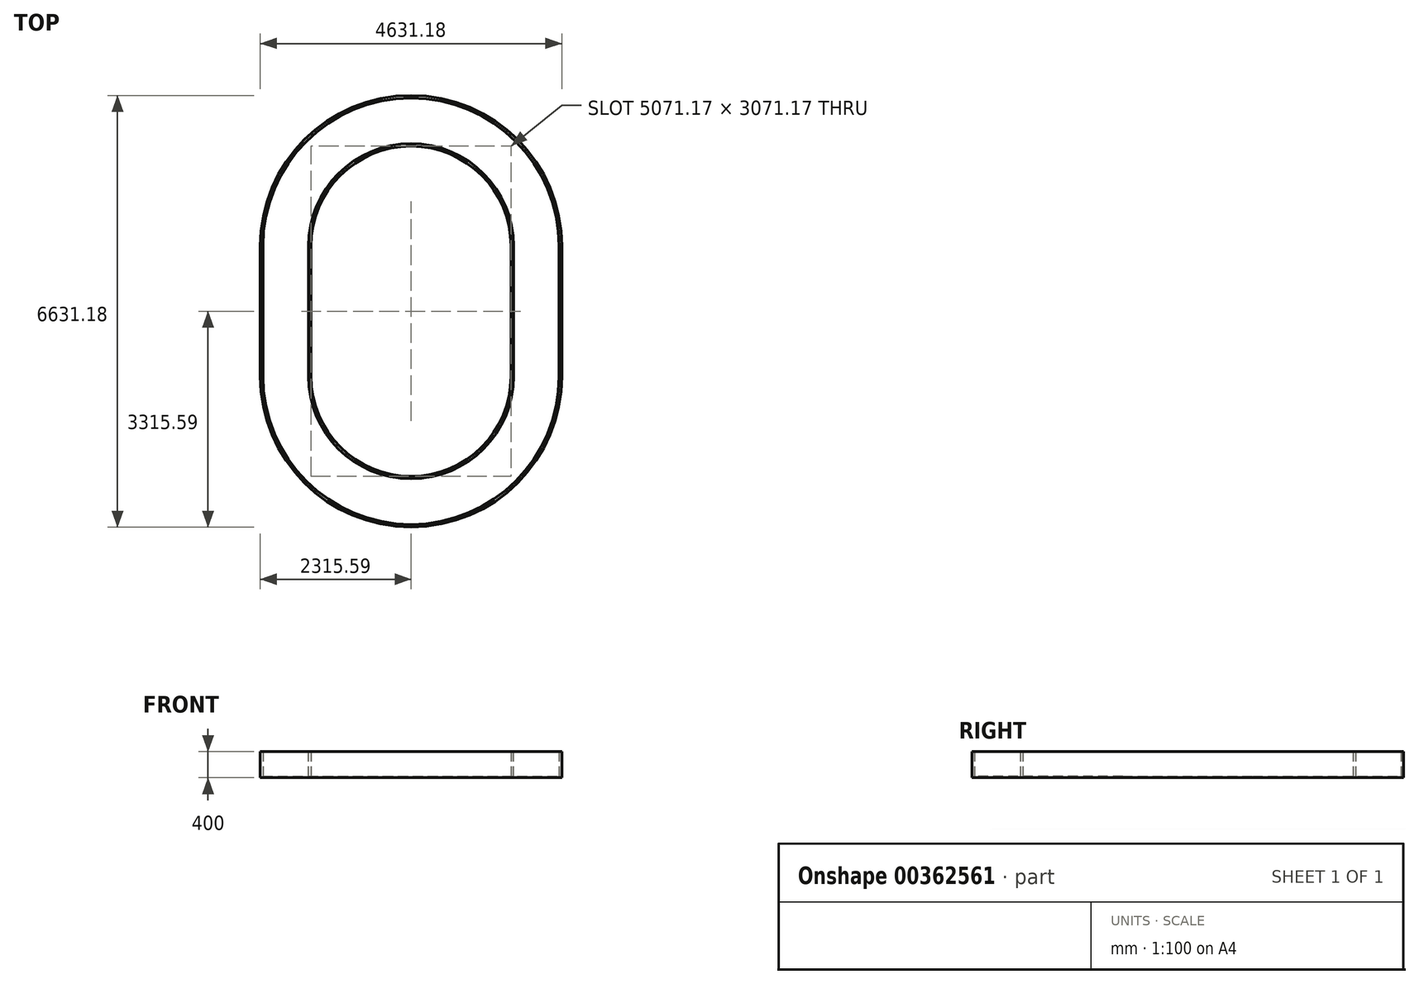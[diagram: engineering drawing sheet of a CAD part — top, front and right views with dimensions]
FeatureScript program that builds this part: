
annotation { "Feature Type Name" : "Feature", "Feature Type Description" : "" }
export const myFeature = defineFeature(function(context is Context, id is Id, definition is map)
    precondition{}
    {
        {
            var Q0;
            Q0=qCreatedBy(makeId("Top.planeOp"),FACE);
            var sketch = newSketch(context, id + "F0", { "sketchPlane" : qUnion([Q0])});
            skArc(sketch, "E0", {"start": v(-2000, 1000) * mm, "mid": v(0, 3000) * mm, "end": v(2000, 1000) * mm});
            skLineSegment(sketch, "E1", {"start": v(-2000, 1000) * mm, "end": v(-2000, 0) * mm});
            skLineSegment(sketch, "E2", {"start": v(2000, 1000) * mm, "end": v(2000, 0) * mm});
            skLineSegment(sketch, "E3.MirrorCS", {"start": v(2000, -1000) * mm, "end": v(2000, 0) * mm});
            skArc(sketch, "E4.MirrorCS", {"start": v(-2000, -1000) * mm, "mid": v(0, -3000) * mm, "end": v(2000, -1000) * mm});
            skLineSegment(sketch, "E5.MirrorCS", {"start": v(-2000, -1000) * mm, "end": v(-2000, 0) * mm});
            skSolve(sketch);
        }
        {
            var Q0;
            Q0=qCreatedBy(makeId("Front.planeOp"),FACE);
            var sketch = newSketch(context, id + "F1", { "sketchPlane" : qUnion([Q0])});
            skLineSegment(sketch, "E6", {"start": v(1925.59, 0) * mm, "end": v(1925.59, -20) * mm, "construction": true});
            skLineSegment(sketch, "E7", {"start": v(1925.59, -20) * mm, "end": v(2315.59, -20) * mm});
            skLineSegment(sketch, "E8", {"start": v(2315.59, -20) * mm, "end": v(2315.59, 380) * mm});
            skLineSegment(sketch, "E9", {"start": v(2315.59, 380) * mm, "end": v(2275.59, 380) * mm});
            skLineSegment(sketch, "E10", {"start": v(2275.59, 380) * mm, "end": v(2275.59, 0) * mm});
            skLineSegment(sketch, "E11", {"start": v(2275.59, 0) * mm, "end": v(1575.59, 0) * mm});
            skLineSegment(sketch, "E12", {"start": v(1575.59, 0) * mm, "end": v(1575.59, 380) * mm});
            skLineSegment(sketch, "E13", {"start": v(1575.59, 380) * mm, "end": v(1535.59, 380) * mm});
            skLineSegment(sketch, "E14", {"start": v(1535.59, 380) * mm, "end": v(1535.59, -20) * mm});
            skLineSegment(sketch, "E15", {"start": v(1535.59, -20) * mm, "end": v(1925.59, -20) * mm});
            skSolve(sketch);
        }
        {
            var Q0;
            Q0 = qSketchRegion(id + "F1", true);
            var Q1;
            Q1 = qConstructionFilter(qBodyType(qCreatedBy(id + "F0" ,EDGE), BodyType.WIRE), ConstructionObject.NO);
            sweep(context, id + "F2", {"profiles" : qUnion([Q0]), "path" : qUnion([Q1])});
        }
    });
